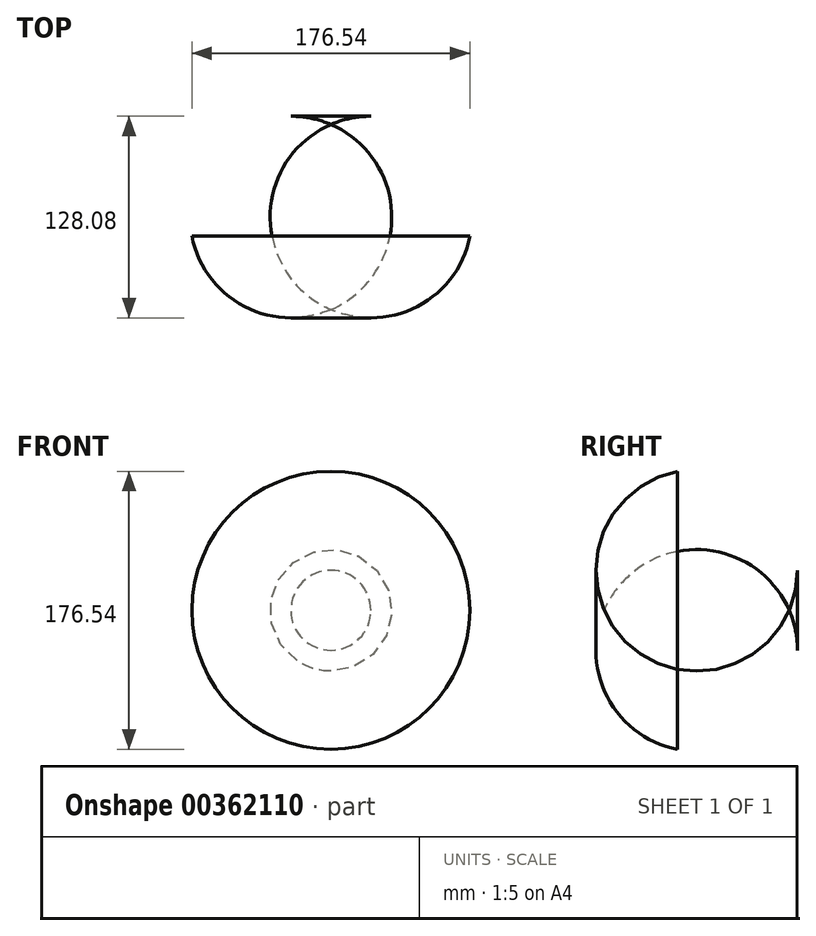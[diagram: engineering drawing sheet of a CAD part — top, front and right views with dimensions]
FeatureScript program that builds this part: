
annotation { "Feature Type Name" : "Feature", "Feature Type Description" : "" }
export const myFeature = defineFeature(function(context is Context, id is Id, definition is map)
    precondition{}
    {
        {
            var Q0;
            Q0=qCreatedBy(makeId("Top.planeOp"),FACE);
            var sketch = newSketch(context, id + "F0", { "sketchPlane" : qUnion([Q0])});
            skLineSegment(sketch, "E0", {"start": v(0, 76.2) * mm, "end": v(-25.4, 76.2) * mm});
            skLineSegment(sketch, "E1", {"start": v(0, 76.2) * mm, "end": v(25.4, 76.2) * mm});
            skArc(sketch, "E2", {"start": v(-25.4, 76.2) * mm, "mid": v(-74.8, 52.92) * mm, "end": v(-88.27, 0) * mm});
            skSolve(sketch);
        }
        {
            var Q0;
            Q0=qCreatedBy(makeId("Top.planeOp"),FACE);
            var sketch = newSketch(context, id + "F1", { "sketchPlane" : qUnion([Q0])});
            skLineSegment(sketch, "E3", {"start": v(0, 0) * mm, "end": v(0, 76.2) * mm});
            skSolve(sketch);
        }
        {
            var Q0;
            Q0=sQuery(id+"F0.wireOp",EDGE,"E2");
            var Q1;
            Q1=sQuery(id+"F1.wireOp",EDGE,"E3");
            revolve(context, id + "F2", {"bodyType" : ToolBodyType.SURFACE, "surfaceEntities" : qUnion([Q0]), "axis" : qUnion([Q1]), "revolveType" : RevolveType.FULL});
        }
    });
